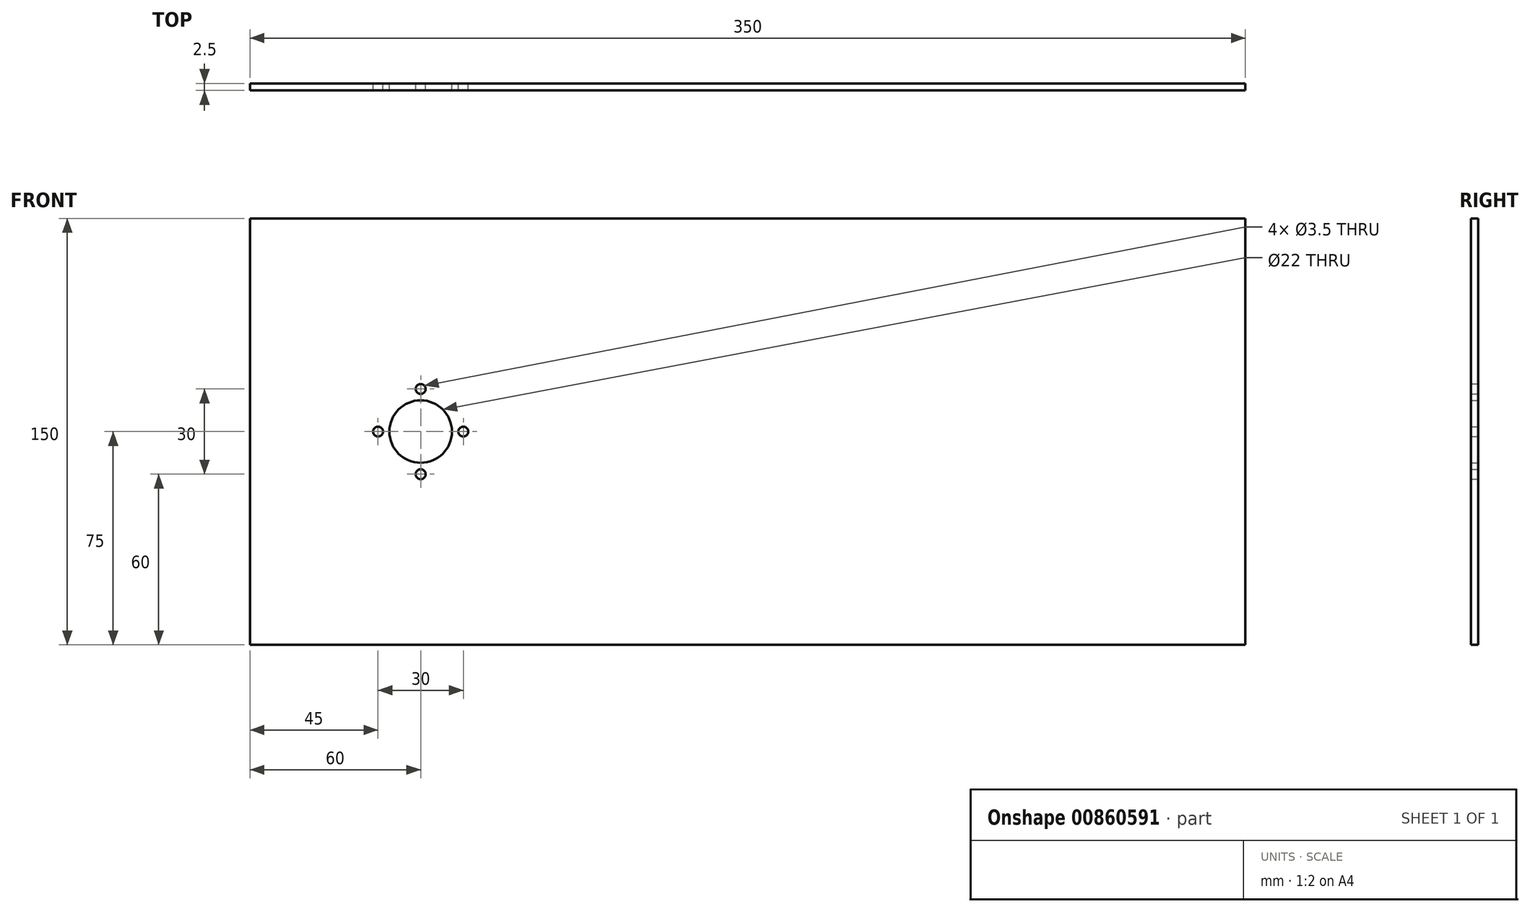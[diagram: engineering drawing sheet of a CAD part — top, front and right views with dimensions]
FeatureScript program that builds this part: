
annotation { "Feature Type Name" : "Feature", "Feature Type Description" : "" }
export const myFeature = defineFeature(function(context is Context, id is Id, definition is map)
    precondition{}
    {
        {
            var Q0;
            Q0=qCreatedBy(makeId("Front.planeOp"),FACE);
            var sketch = newSketch(context, id + "F0", { "sketchPlane" : qUnion([Q0])});
            skLineSegment(sketch, "E0.bottom", {"start": v(175, 75) * mm, "end": v(-175, 75) * mm});
            skLineSegment(sketch, "E0.top", {"start": v(175, -75) * mm, "end": v(-175, -75) * mm});
            skLineSegment(sketch, "E0.left", {"start": v(175, 75) * mm, "end": v(175, -75) * mm});
            skLineSegment(sketch, "E0.right", {"start": v(-175, 75) * mm, "end": v(-175, -75) * mm});
            skPoint(sketch, "E0.middle", {"position": v(0, 0) * mm});
            skCircle(sketch, "E1", {"center": v(-115, 0) * mm, "radius": 11 * mm});
            skCircle(sketch, "E2", {"center": v(-130, 0) * mm, "radius": 1.75 * mm});
            skCircle(sketch, "E3.1.0", {"center": v(-115, -15) * mm, "radius": 1.75 * mm});
            skCircle(sketch, "E3.2.0", {"center": v(-100, 0) * mm, "radius": 1.75 * mm});
            skCircle(sketch, "E3.3.0", {"center": v(-115, 15) * mm, "radius": 1.75 * mm});
            skSolve(sketch);
        }
        {
            var Q0;
            Q0 = qSketchRegion(id + "F0", true);
            extrude(context, id + "F1", {"entities" : qUnion([Q0]), "depth" : 2.5 * mm, "offsetDistance" : 25 * mm});
        }
    });
